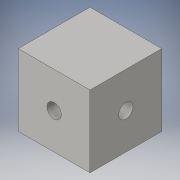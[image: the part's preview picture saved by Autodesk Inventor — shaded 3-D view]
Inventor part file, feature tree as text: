
AUTODESK INVENTOR PART (.ipt)
format: ipt  version: 2016 (Build 200138000, 138)  size: 244,736 bytes
history: native  units: in
note: dims shown in document units (in); Inventor stores cm internally (conversion verified against a paired STEP export)
features: extrude x3, sketch x3
ambient origin geometry x8: Origin, YZ Plane, XZ Plane, XY Plane, X Axis, Y Axis, Z Axis, Center Point
bodies: Solid1 (feature_tree)
feature tree (6):
  extrude  "Extrusion1"  Depth=0.9843in
  extrude  "Extrusion2"  Depth=0.9843in
  extrude  "Extrusion3"  Depth=0.9843in
  sketch  "Sketch1"  dims[d0=0.9843in d1=0.9843in]
  sketch  "Sketch2"  dims[d2=0.9843in d3=0.0in d4=0.1969in]
  sketch  "Sketch3"  dims[d5=0.9843in d6=0.0in d7=0.1969in d8=0.9843in d9=0.0in]
